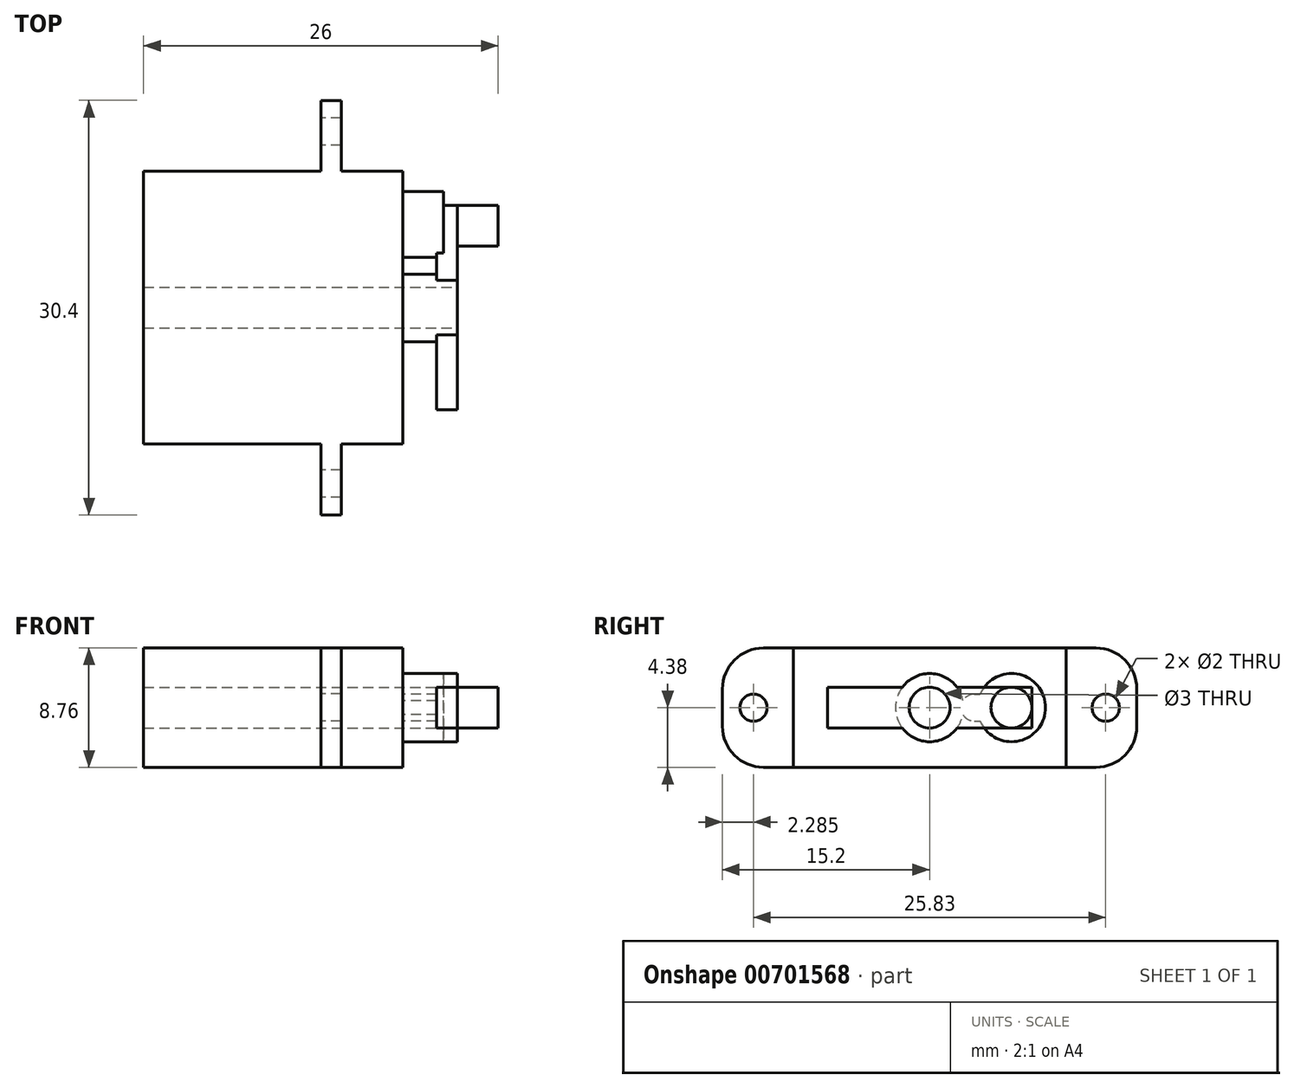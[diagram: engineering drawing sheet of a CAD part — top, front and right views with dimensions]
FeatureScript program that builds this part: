
annotation { "Feature Type Name" : "Feature", "Feature Type Description" : "" }
export const myFeature = defineFeature(function(context is Context, id is Id, definition is map)
    precondition{}
    {
        {
            var Q0;
            Q0=qCreatedBy(makeId("Top.planeOp"),FACE);
            var sketch = newSketch(context, id + "F0", { "sketchPlane" : qUnion([Q0])});
            skLineSegment(sketch, "E0.bottom", {"start": v(-19, 10) * mm, "end": v(0, 10) * mm});
            skLineSegment(sketch, "E0.top", {"start": v(-19, -10) * mm, "end": v(0, -10) * mm});
            skLineSegment(sketch, "E0.left", {"start": v(-19, 10) * mm, "end": v(-19, -10) * mm});
            skLineSegment(sketch, "E0.right", {"start": v(0, 10) * mm, "end": v(0, -10) * mm});
            skPoint(sketch, "E1", {"position": v(-19, 0) * mm});
            skSolve(sketch);
        }
        {
            var Q0;
            Q0 = qSketchRegion(id + "F0", true);
            extrude(context, id + "F1", {"entities" : qUnion([Q0]), "endBound" : BoundingType.SYMMETRIC, "depth" : 8.75 * mm, "offsetDistance" : 25 * mm});
        }
        {
            var Q0;
            Q0=makeQuery(id+"F1.opExtrude","SWEPT_FACE",FACE,{"disambiguationData":[OSD([sQuery(id+"F0.wireOp",EDGE,"E0.right")])]});
            cPlane(context, id + "F2", {"entities" : qUnion([Q0]), "cplaneType" : CPlaneType.OFFSET, "offset" : 6 * mm, "oppositeDirection" : true, "width" : 150 * mm, "height" : 150 * mm});
        }
        {
            var Q0;
            Q0=qCreatedBy(id+"F2.planeOp",FACE);
            var sketch = newSketch(context, id + "F3", { "sketchPlane" : qUnion([Q0])});
            skLineSegment(sketch, "E2.bottom", {"start": v(15.2, 4.38) * mm, "end": v(-15.2, 4.38) * mm});
            skLineSegment(sketch, "E2.top", {"start": v(15.2, -4.38) * mm, "end": v(-15.2, -4.38) * mm});
            skLineSegment(sketch, "E2.left", {"start": v(15.2, 4.38) * mm, "end": v(15.2, -4.38) * mm});
            skLineSegment(sketch, "E2.right", {"start": v(-15.2, 4.38) * mm, "end": v(-15.2, -4.38) * mm});
            skPoint(sketch, "E2.middle", {"position": v(0, 0) * mm});
            skCircle(sketch, "E3", {"center": v(-12.91, 0) * mm, "radius": 1 * mm});
            skLineSegment(sketch, "E4", {"start": v(0, -1.86) * mm, "end": v(0, -3.61) * mm, "construction": true});
            skCircle(sketch, "E5.MirrorC", {"center": v(12.91, 0) * mm, "radius": 1 * mm});
            skSolve(sketch);
        }
        {
            var Q0;
            Q0 = qSketchRegion(id + "F3", true);
            extrude(context, id + "F4", {"entities" : qUnion([Q0]), "operationType" : NewBodyOperationType.ADD, "depth" : 1.5 * mm, "offsetDistance" : 25 * mm});
        }
        {
            var Q0;
            Q0=makeQuery(id+"F1.opExtrude","SWEPT_FACE",FACE,{"disambiguationData":[OSD([sQuery(id+"F0.wireOp",EDGE,"E0.right")])]});
            var sketch = newSketch(context, id + "F5", { "sketchPlane" : qUnion([Q0])});
            skCircle(sketch, "E6", {"center": v(6, 0) * mm, "radius": 2.5 * mm});
            skArc(sketch, "E7", {"start": v(3.29, 0.99) * mm, "mid": v(2.3, 0) * mm, "end": v(3.29, -0.99) * mm});
            skLineSegment(sketch, "E8", {"start": v(3.29, 0) * mm, "end": v(3.29, 1.13) * mm, "construction": true});
            skLineSegment(sketch, "E9", {"start": v(3.29, -0.99) * mm, "end": v(3.7, -0.99) * mm});
            skLineSegment(sketch, "E10", {"start": v(3.29, 0.99) * mm, "end": v(3.7, 0.99) * mm});
            skSolve(sketch);
        }
        {
            var Q0;
            Q0 = qSketchRegion(id + "F5", true);
            extrude(context, id + "F6", {"entities" : qUnion([Q0]), "operationType" : NewBodyOperationType.ADD, "depth" : 3 * mm, "offsetDistance" : 25 * mm});
        }
        {
            var Q0;
            Q0=makeQuery(id+"F6.opExtrude","CAP_FACE",FACE,{"disambiguationData":[OSD([sQuery(id+"F5.wireOp",EDGE,"E6"),sQuery(id+"F5.wireOp",EDGE,"E7"),sQuery(id+"F5.wireOp",EDGE,"E9"),sQuery(id+"F5.wireOp",EDGE,"E10")])],"isStart":false});
            var sketch = newSketch(context, id + "F7", { "sketchPlane" : qUnion([Q0])});
            skCircle(sketch, "E11", {"center": v(6, 0) * mm, "radius": 1.5 * mm});
            skSolve(sketch);
        }
        {
            var Q0;
            Q0 = qSketchRegion(id + "F7", true);
            extrude(context, id + "F8", {"entities" : qUnion([Q0]), "operationType" : NewBodyOperationType.ADD, "depth" : 4 * mm, "offsetDistance" : 25 * mm});
        }
        {
            var Q0;
            Q0=qCreatedBy(makeId("Right.planeOp"),FACE);
            var sketch = newSketch(context, id + "F9", { "sketchPlane" : qUnion([Q0])});
            skCircle(sketch, "E12", {"center": v(0, 0) * mm, "radius": 2.5 * mm});
            skSolve(sketch);
        }
        {
            var Q0;
            Q0 = qSketchRegion(id + "F9", true);
            extrude(context, id + "F10", {"entities" : qUnion([Q0]), "depth" : 4 * mm, "offsetDistance" : 25 * mm});
        }
        {
            var Q0;
            Q0=makeQuery(id+"F10.opExtrude","CAP_FACE",FACE,{"disambiguationData":[OSD([sQuery(id+"F9.wireOp",EDGE,"E12")])],"isStart":false});
            var sketch = newSketch(context, id + "F11", { "sketchPlane" : qUnion([Q0])});
            skCircle(sketch, "E13", {"center": v(0, 0) * mm, "radius": 1.5 * mm});
            skSolve(sketch);
        }
        {
            var Q0;
            Q0=makeQuery(id+"F10.opExtrude","CAP_FACE",FACE,{"disambiguationData":[OSD([sQuery(id+"F9.wireOp",EDGE,"E12")])],"isStart":false});
            var sketch = newSketch(context, id + "F12", { "sketchPlane" : qUnion([Q0])});
            skLineSegment(sketch, "E14.bottom", {"start": v(-7.5, 1.5) * mm, "end": v(7.5, 1.5) * mm});
            skLineSegment(sketch, "E14.top", {"start": v(-7.5, -1.5) * mm, "end": v(7.5, -1.5) * mm});
            skLineSegment(sketch, "E14.left", {"start": v(-7.5, 1.5) * mm, "end": v(-7.5, -1.5) * mm});
            skLineSegment(sketch, "E14.right", {"start": v(7.5, 1.5) * mm, "end": v(7.5, -1.5) * mm});
            skPoint(sketch, "E14.middle", {"position": v(0, 0) * mm});
            skSolve(sketch);
        }
        {
            var Q0;
            Q0 = qSketchRegion(id + "F12", true);
            extrude(context, id + "F13", {"entities" : qUnion([Q0]), "operationType" : NewBodyOperationType.ADD, "oppositeDirection" : true, "depth" : 1.5 * mm, "offsetDistance" : 25 * mm});
        }
        {
            var Q0;
            Q0 = qSketchRegion(id + "F11", true);
            extrude(context, id + "F14", {"entities" : qUnion([Q0]), "operationType" : NewBodyOperationType.REMOVE, "oppositeDirection" : true, "depth" : 25 * mm, "offsetDistance" : 25 * mm});
        }
        {
            var Q0;
            Q0=makeQuery(id+"F4.opExtrude","SWEPT_EDGE",EDGE,{"disambiguationData":[OSD([sQuery(id+"F3.wireOp",EDGE,"E2.top"),sQuery(id+"F3.wireOp",EDGE,"E2.right")])]});
            var Q1;
            Q1=makeQuery(id+"F4.opExtrude","SWEPT_EDGE",EDGE,{"disambiguationData":[OSD([sQuery(id+"F3.wireOp",EDGE,"E2.bottom"),sQuery(id+"F3.wireOp",EDGE,"E2.right")])]});
            var Q2;
            Q2=makeQuery(id+"F4.opExtrude","SWEPT_EDGE",EDGE,{"disambiguationData":[OSD([sQuery(id+"F3.wireOp",EDGE,"E2.top"),sQuery(id+"F3.wireOp",EDGE,"E2.left")])]});
            var Q3;
            Q3=makeQuery(id+"F4.opExtrude","SWEPT_EDGE",EDGE,{"disambiguationData":[OSD([sQuery(id+"F3.wireOp",EDGE,"E2.bottom"),sQuery(id+"F3.wireOp",EDGE,"E2.left")])]});
            fillet(context, id + "F15", {"entities" : qUnion([Q0, Q1, Q2, Q3]), "radius" : 3 * mm, "tangentPropagation" : true, "allowEdgeOverflow" : false});
        }
    });
